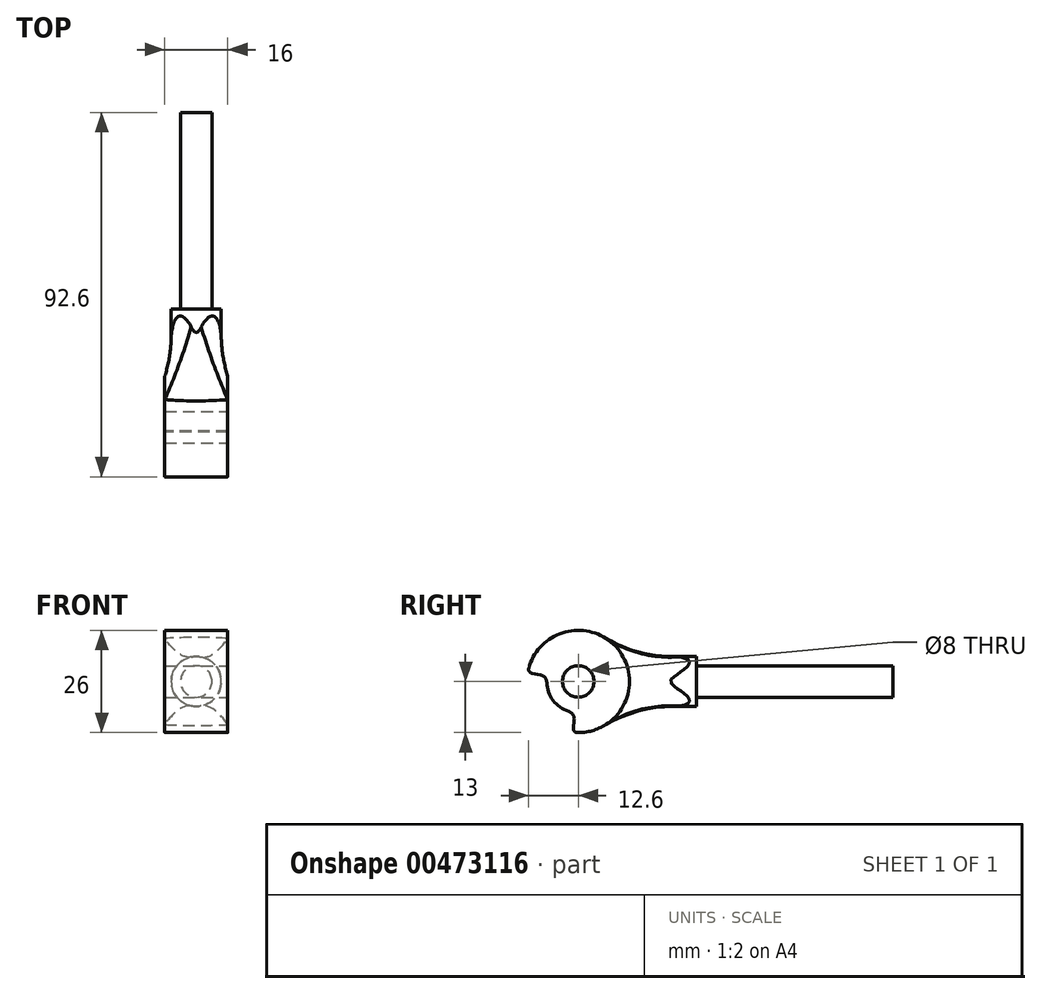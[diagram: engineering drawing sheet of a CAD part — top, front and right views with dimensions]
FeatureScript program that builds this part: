
annotation { "Feature Type Name" : "Feature", "Feature Type Description" : "" }
export const myFeature = defineFeature(function(context is Context, id is Id, definition is map)
    precondition{}
    {
        {
            var Q0;
            Q0=qCreatedBy(makeId("Right.planeOp"),FACE);
            var sketch = newSketch(context, id + "F0", { "sketchPlane" : qUnion([Q0])});
            skArc(sketch, "E0", {"start": v(-0.28, -13) * mm, "mid": v(10.38, 7.82) * mm, "end": v(-12.57, 3.32) * mm});
            skArc(sketch, "E1", {"start": v(-8, -0.21) * mm, "mid": v(-6.39, -4.81) * mm, "end": v(-2.41, -7.63) * mm});
            skLineSegment(sketch, "E2", {"start": v(-1.02, -9.74) * mm, "end": v(-1.25, -11.9) * mm});
            skLineSegment(sketch, "E3", {"start": v(-9.65, 1.7) * mm, "end": v(-11.78, 2.08) * mm});
            skPoint(sketch, "E4.visualSharp", {"position": v(-7.88, 1.39) * mm});
            skArc(sketch, "E4.filletArc", {"start": v(-8, -0.21) * mm, "mid": v(-8.48, 1.04) * mm, "end": v(-9.65, 1.7) * mm});
            skPoint(sketch, "E5.visualSharp", {"position": v(-0.84, -7.96) * mm});
            skArc(sketch, "E5.filletArc", {"start": v(-1.02, -9.74) * mm, "mid": v(-1.34, -8.44) * mm, "end": v(-2.41, -7.63) * mm});
            skPoint(sketch, "E6.visualSharp", {"position": v(-12.8, 2.26) * mm});
            skArc(sketch, "E6.filletArc", {"start": v(-12.57, 3.32) * mm, "mid": v(-12.45, 2.52) * mm, "end": v(-11.78, 2.08) * mm});
            skPoint(sketch, "E7.visualSharp", {"position": v(-1.36, -12.93) * mm});
            skArc(sketch, "E7.filletArc", {"start": v(-1.25, -11.9) * mm, "mid": v(-1, -12.66) * mm, "end": v(-0.28, -13) * mm});
            skSolve(sketch);
        }
        {
            var Q0;
            Q0=qSketchRegion(id+"F0",true);
            extrude(context, id + "F1", {"entities" : qUnion([Q0]), "depth" : 8 * mm, "hasSecondDirection" : true, "secondDirectionOppositeDirection" : true, "secondDirectionDepth" : 8 * mm, "offsetDistance" : 25 * mm});
        }
        {
            var Q0;
            Q0=qCreatedBy(makeId("Front.planeOp"),FACE);
            var sketch = newSketch(context, id + "F2", { "sketchPlane" : qUnion([Q0])});
            skCircle(sketch, "E8", {"center": v(0, 0) * mm, "radius": 6.35 * mm});
            skSolve(sketch);
        }
        {
            var Q0;
            Q0=qSketchRegion(id+"F2",true);
            extrude(context, id + "F3", {"entities" : qUnion([Q0]), "operationType" : NewBodyOperationType.ADD, "oppositeDirection" : true, "depth" : 80 * mm});
        }
        {
            var Q0;
            Q0=makeQuery(id+"F3.boolean.opBoolean","INTERSECT",EDGE,{"derivedFrom":[makeQuery(id+"F1.opExtrude","SWEPT_FACE",FACE,{"disambiguationData":[OSD([sQuery(id+"F0.wireOp",EDGE,"E0")])]}),makeQuery(id+"F3.opExtrude","SWEPT_FACE",FACE,{"disambiguationData":[OSD([sQuery(id+"F2.wireOp",EDGE,"E8")])]})]});
            fillet(context, id + "F4", {"entities" : qUnion([Q0]), "radius" : 34 * mm, "tangentPropagation" : true, "allowEdgeOverflow" : false});
        }
        {
            var Q0;
            Q0=makeQuery(id+"F3.opExtrude","CAP_FACE",FACE,{"disambiguationData":[OSD([sQuery(id+"F2.wireOp",EDGE,"E8")])],"isStart":false});
            var sketch = newSketch(context, id + "F5", { "sketchPlane" : qUnion([Q0])});
            skCircle(sketch, "E9", {"center": v(0, 0) * mm, "radius": 4 * mm});
            skCircle(sketch, "E10", {"center": v(0, 0) * mm, "radius": 6.35 * mm});
            skSolve(sketch);
        }
        {
            var Q0;
            Q0=qSketchRegion(id+"F5",true);
            extrude(context, id + "F6", {"entities" : qUnion([Q0]), "operationType" : NewBodyOperationType.REMOVE, "oppositeDirection" : true, "depth" : 50 * mm});
        }
        {
            var Q0;
            Q0=makeQuery(id+"F1.opExtrude","CAP_FACE",FACE,{"disambiguationData":[OSD([sQuery(id+"F0.wireOp",EDGE,"E0")])],"isStart":false});
            var sketch = newSketch(context, id + "F7", { "sketchPlane" : qUnion([Q0])});
            skCircle(sketch, "E11", {"center": v(0, 0) * mm, "radius": 4 * mm});
            skSolve(sketch);
        }
        {
            var Q0;
            Q0=qSketchRegion(id+"F7",true);
            extrude(context, id + "F8", {"entities" : qUnion([Q0]), "operationType" : NewBodyOperationType.REMOVE, "oppositeDirection" : true, "depth" : 16 * mm});
        }
    });
